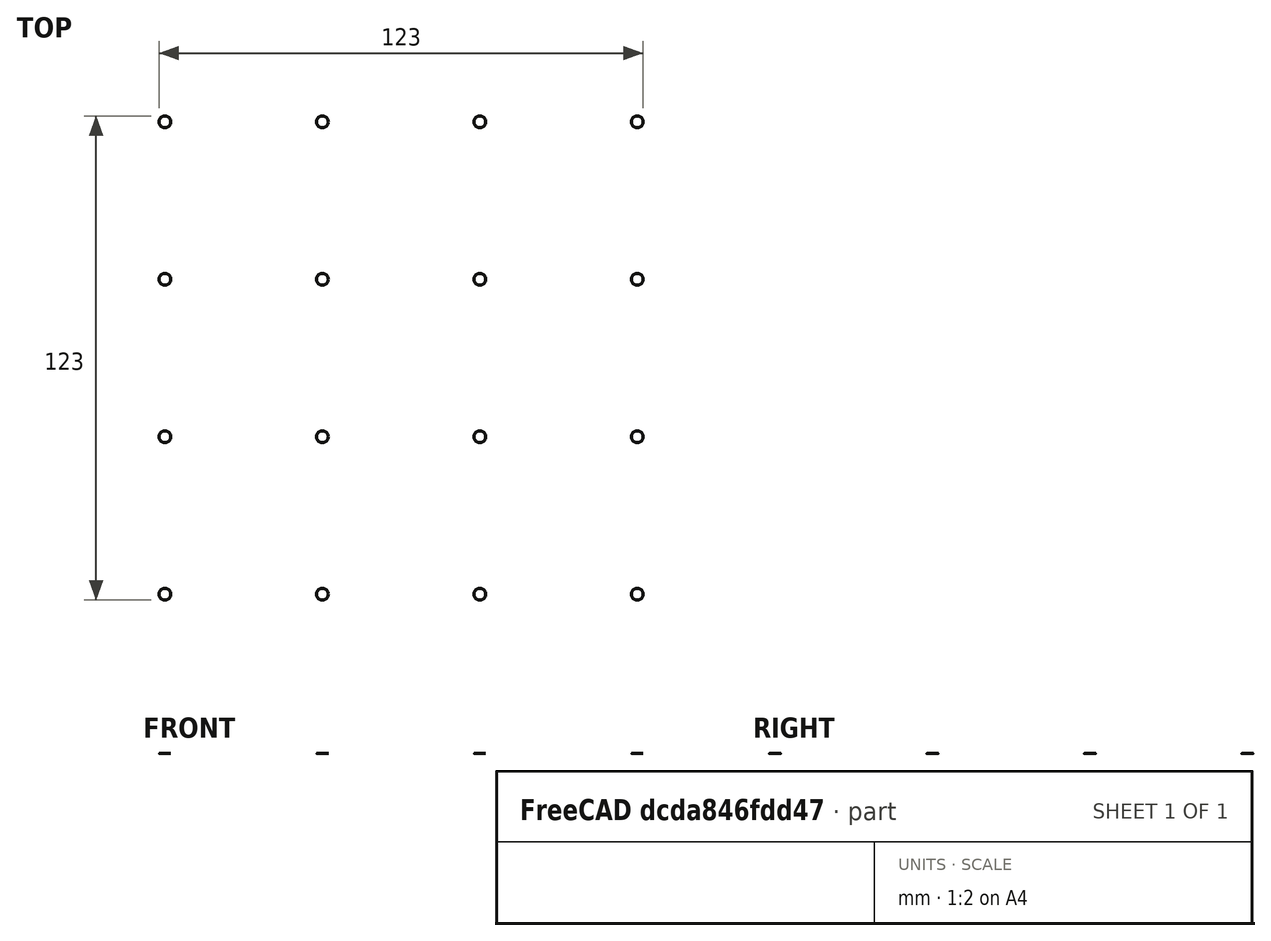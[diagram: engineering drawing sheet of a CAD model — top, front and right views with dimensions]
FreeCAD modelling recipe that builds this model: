
FCSTD DOCUMENT  (FreeCAD 0.16RUnknown)
Label: board_with_holes
License: All rights reserved
LicenseURL: http://en.wikipedia.org/wiki/All_rights_reserved
objects: App::FeaturePython×4, Part::Part2DObjectPython×2, App::DocumentObjectGroup×2, Part::FeaturePython×1
note: 3 computed .brp shape members not serialized (recipe doc carries the construction recipe); baked Part::Feature solids carry a one-line shape summary decoded from their .brp

FEATURE [Part::Part2DObjectPython] Rectangle  label="BoardShape"  # Draft 2D object (typed FeaturePython)
  ChamferSize = 0
  Columns = 1
  FilletRadius = 0
  Height = 50
  Length = 75
  MakeFace = true
  Placement = pos=(0,0,-5) rot=(0,0,1;0rad)
  Rows = 1
FEATURE [App::FeaturePython] Dimension002  label="Dim Board X"  # Draft dimension (typed FeaturePython)
  Dimline = (85,0,0)
  Direction = (0,1,0)
  Distance = 50
  End = (75,50,0)
  Normal = (0,0,1)
  Start = (75,0,0)
FEATURE [App::FeaturePython] Dimension003  label="Dim Board Y"  # Draft dimension (typed FeaturePython)
  Dimline = (0,60,0)
  Direction = (1,0,0)
  Distance = 75
  End = (75,50,0)
  Normal = (0,0,1)
  Start = (0,50,0)
FEATURE [Part::Part2DObjectPython] Circle  # Draft 2D object (typed FeaturePython)
  FirstAngle = 0
  LastAngle = 0
  MakeFace = true
  Placement = pos=(-22.5,-35,1) rot=(0,0,1;0rad)
  Radius = 1.5
FEATURE [Part::FeaturePython] Array  # Draft array (typed FeaturePython)
  Angle = 360
  ArrayType = 0
  Axis = (0,0,1)
  Base = -> Circle
  Center = (0,0,0)
  Fuse = false
  IntervalAxis = (0,0,0)
  IntervalX = (40,0,0)
  IntervalY = (0,40,0)
  IntervalZ = (0,0,0)
  NumberPolar = 1
  NumberX = 4
  NumberY = 4
  NumberZ = 1
FEATURE [App::DocumentObjectGroup] Groupe  label="Board"
  Group = -> [Rectangle,Dimension002,Dimension003]
FEATURE [App::FeaturePython] Dimension004  label="Dim Hole X"  # Draft dimension (typed FeaturePython)
  Dimline = (0,-35,10)
  Direction = (1,0,0)
  Distance = 40
  End = (17.5,-35,10)
  Normal = (0,0,1)
  Start = (-22.5,-35,10)
FEATURE [App::FeaturePython] Dimension005  label="Dim Hole Y"  # Draft dimension (typed FeaturePython)
  Dimline = (-22.5,-35,10)
  Direction = (0,1,0)
  Distance = 40
  End = (-22.5,-35,10)
  Normal = (0,0,1)
  Start = (-22.5,5,10)
FEATURE [App::DocumentObjectGroup] Groupe001  label="Base"
  Group = -> [Array,Dimension004,Dimension005]
